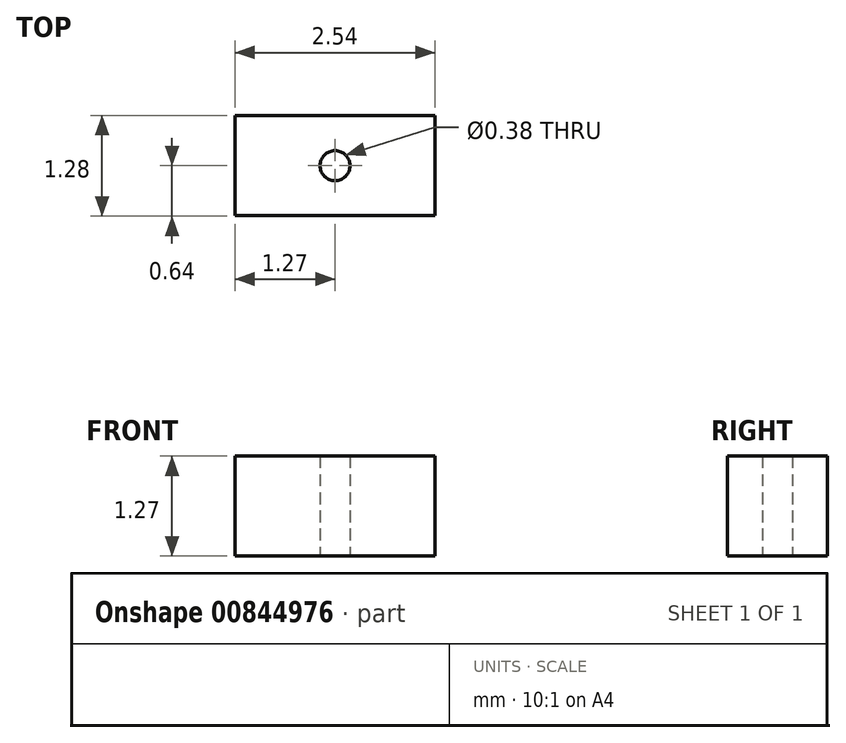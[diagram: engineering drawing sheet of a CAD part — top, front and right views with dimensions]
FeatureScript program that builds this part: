
annotation { "Feature Type Name" : "Feature", "Feature Type Description" : "" }
export const myFeature = defineFeature(function(context is Context, id is Id, definition is map)
    precondition{}
    {
        {
            var Q0;
            Q0=qCreatedBy(makeId("Top.planeOp"),FACE);
            var sketch = newSketch(context, id + "F0", { "sketchPlane" : qUnion([Q0])});
            skLineSegment(sketch, "E0.bottom", {"start": v(1.27, -0.64) * mm, "end": v(-1.27, -0.64) * mm});
            skLineSegment(sketch, "E0.top", {"start": v(1.27, 0.64) * mm, "end": v(-1.27, 0.64) * mm});
            skLineSegment(sketch, "E0.left", {"start": v(1.27, -0.63) * mm, "end": v(1.27, 0.64) * mm});
            skLineSegment(sketch, "E0.right", {"start": v(-1.27, -0.64) * mm, "end": v(-1.27, 0.64) * mm});
            skPoint(sketch, "E0.middle", {"position": v(0, 0) * mm});
            skCircle(sketch, "E1", {"center": v(0, 0) * mm, "radius": 0.2 * mm});
            skSolve(sketch);
        }
        {
            var Q0;
            Q0 = qSketchRegion(id + "F0", true);
            extrude(context, id + "F1", {"entities" : qUnion([Q0]), "depth" : 1.27 * mm, "offsetDistance" : 25.4 * mm});
        }
    });
